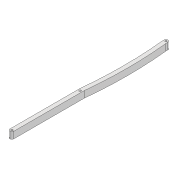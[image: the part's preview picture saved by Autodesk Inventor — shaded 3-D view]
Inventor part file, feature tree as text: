
AUTODESK INVENTOR PART (.ipt)
format: ipt  version: 2022 (Build 260153000, 153)  size: 102,912 bytes
history: native  units: mm
features: extrude x1, sketch x1
ambient origin geometry x8: Origin, YZ Plane, XZ Plane, XY Plane, X Axis, Y Axis, Z Axis, Center Point
bodies: Solid1 (feature_tree)
feature tree (2):
  extrude  "Extrusion1"  Depth=233.234mm
  sketch  "Sketch1"  dims[d0=6.0mm d1=233.234mm d2=3.0mm d3=3.0mm d4=10.0mm d5=0.0mm d16=3.0mm d17=103.234mm d20=600.0mm d21=3.0mm d22=3.0mm d23=600.0mm]
